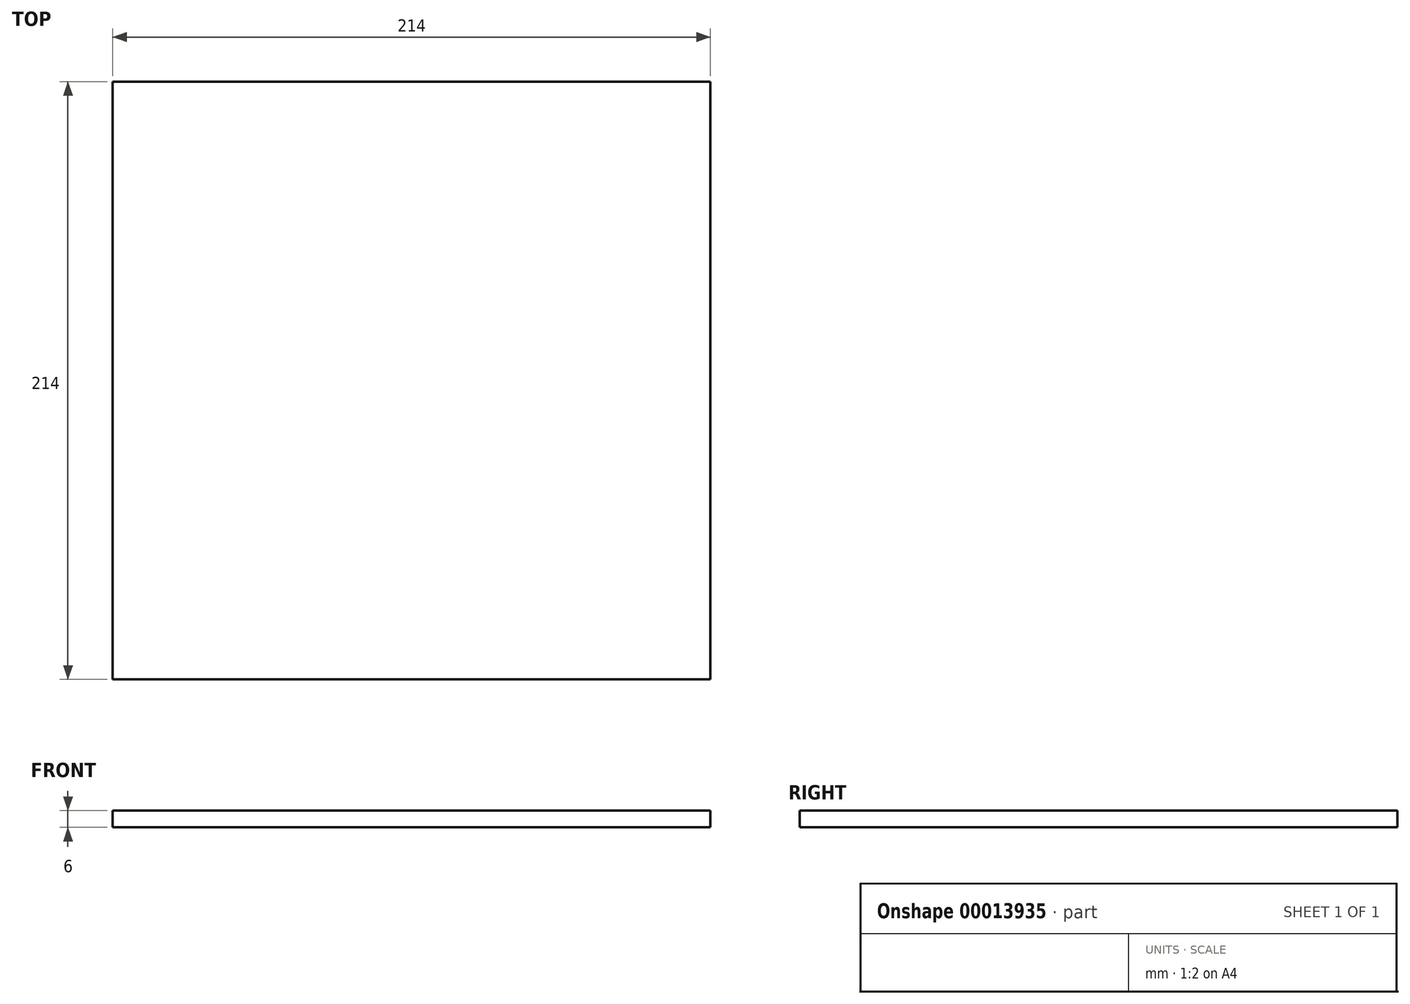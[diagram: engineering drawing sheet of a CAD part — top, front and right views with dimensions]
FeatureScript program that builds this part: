
annotation { "Feature Type Name" : "Feature", "Feature Type Description" : "" }
export const myFeature = defineFeature(function(context is Context, id is Id, definition is map)
    precondition{}
    {
        {
            var Q0;
            Q0=qCreatedBy(makeId("Top.planeOp"),FACE);
            var sketch = newSketch(context, id + "F0", { "sketchPlane" : qUnion([Q0])});
            skLineSegment(sketch, "E0.bottom", {"start": v(0, 0) * mm, "end": v(214, 0) * mm});
            skLineSegment(sketch, "E0.top", {"start": v(0, 214) * mm, "end": v(214, 214) * mm});
            skLineSegment(sketch, "E0.left", {"start": v(0, 0) * mm, "end": v(0, 214) * mm});
            skLineSegment(sketch, "E0.right", {"start": v(214, 0) * mm, "end": v(214, 214) * mm});
            skSolve(sketch);
        }
        {
            var Q0;
            Q0 = qSketchRegion(id + "F0", true);
            extrude(context, id + "F1", {"entities" : qUnion([Q0]), "depth" : 6 * mm});
        }
    });
